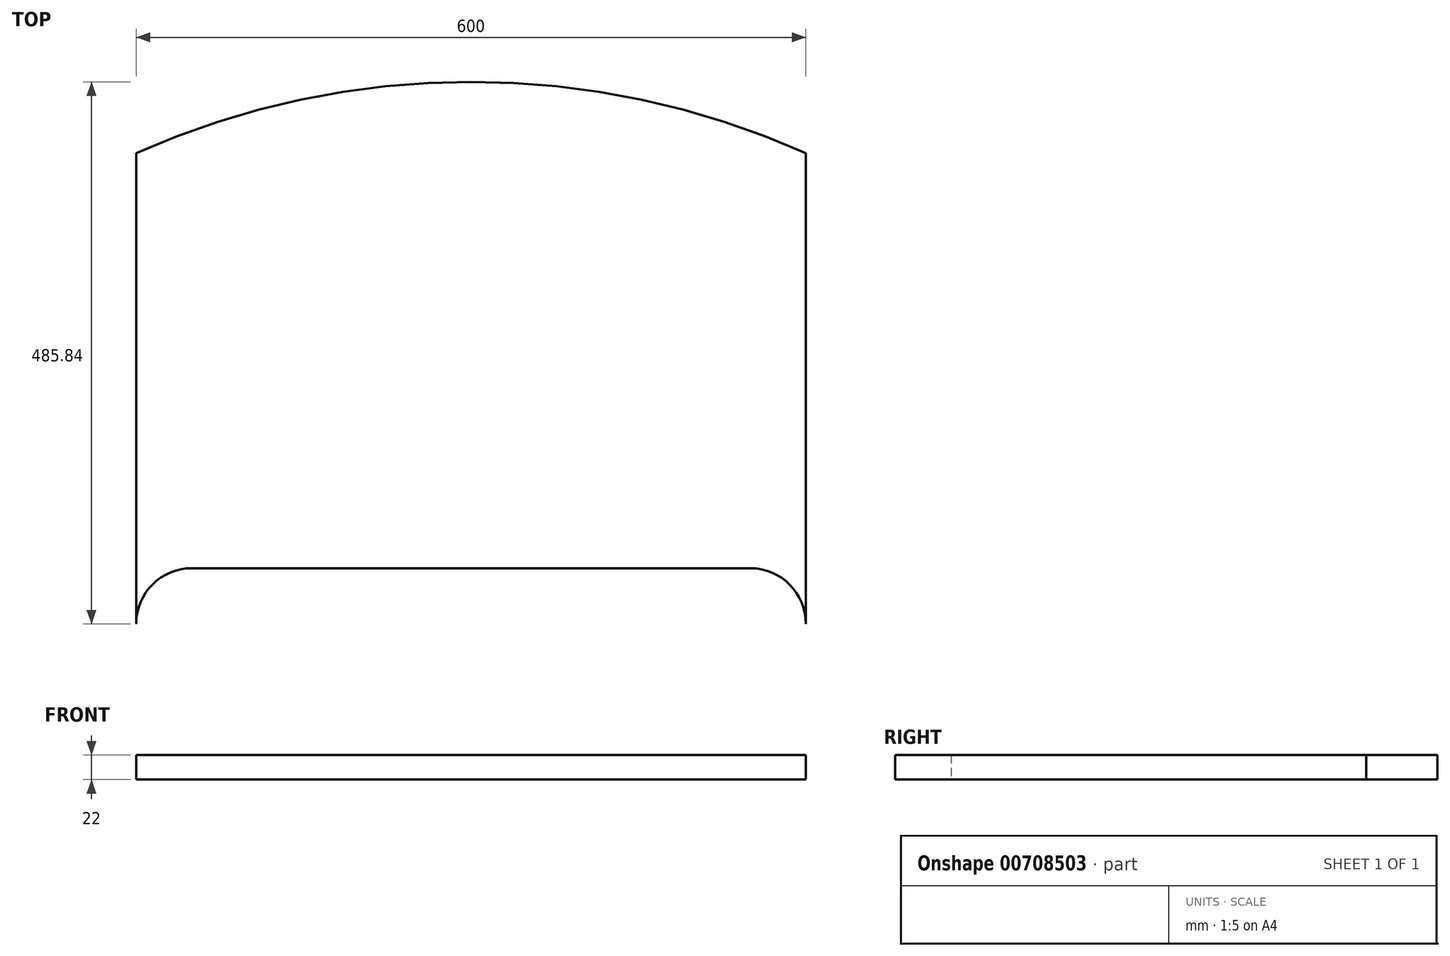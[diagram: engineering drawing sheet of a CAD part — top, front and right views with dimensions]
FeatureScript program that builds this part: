
annotation { "Feature Type Name" : "Feature", "Feature Type Description" : "" }
export const myFeature = defineFeature(function(context is Context, id is Id, definition is map)
    precondition{}
    {
        {
            var Q0;
            Q0=qCreatedBy(makeId("Top.planeOp"),FACE);
            var sketch = newSketch(context, id + "F0", { "sketchPlane" : qUnion([Q0])});
            skLineSegment(sketch, "E0.top", {"start": v(-250, 300) * mm, "end": v(250, 300) * mm});
            skPoint(sketch, "E0.middle", {"position": v(0, 0) * mm});
            skPoint(sketch, "E1.end.orphan", {"position": v(-300, -300) * mm});
            skPoint(sketch, "E2.visualSharp", {"position": v(-300, 300) * mm});
            skArc(sketch, "E2.filletArc", {"start": v(-250, 300) * mm, "mid": v(-285.36, 285.36) * mm, "end": v(-300, 250) * mm});
            skPoint(sketch, "E3.visualSharp", {"position": v(-300, -52.1) * mm});
            skPoint(sketch, "E4.visualSharp", {"position": v(300, 300) * mm});
            skArc(sketch, "E4.filletArc", {"start": v(300, 250) * mm, "mid": v(285.36, 285.36) * mm, "end": v(250, 300) * mm});
            skLineSegment(sketch, "E5", {"start": v(-300, -2.1) * mm, "end": v(-300, -2.1) * mm});
            skArc(sketch, "E6", {"start": v(300, 671.9) * mm, "mid": v(0, 735.84) * mm, "end": v(-300, 671.9) * mm});
            skPoint(sketch, "E7.visualSharp", {"position": v(-300, -74.1) * mm});
            skPoint(sketch, "E8.end.orphan", {"position": v(-732.48, -70.26) * mm});
            skPoint(sketch, "E9.orphan", {"position": v(-734.26, -48.26) * mm});
            skLineSegment(sketch, "E10", {"start": v(300, 250) * mm, "end": v(300, 671.9) * mm});
            skLineSegment(sketch, "E11", {"start": v(-300, 250) * mm, "end": v(-300, 671.9) * mm});
            skPoint(sketch, "E12.start.orphan", {"position": v(300, -300) * mm});
            skSolve(sketch);
        }
        {
            var Q0;
            Q0=qSketchRegion(id+"F0",true);
            extrude(context, id + "F1", {"entities" : qUnion([Q0]), "depth" : 22 * mm, "offsetDistance" : 25 * mm});
        }
    });
